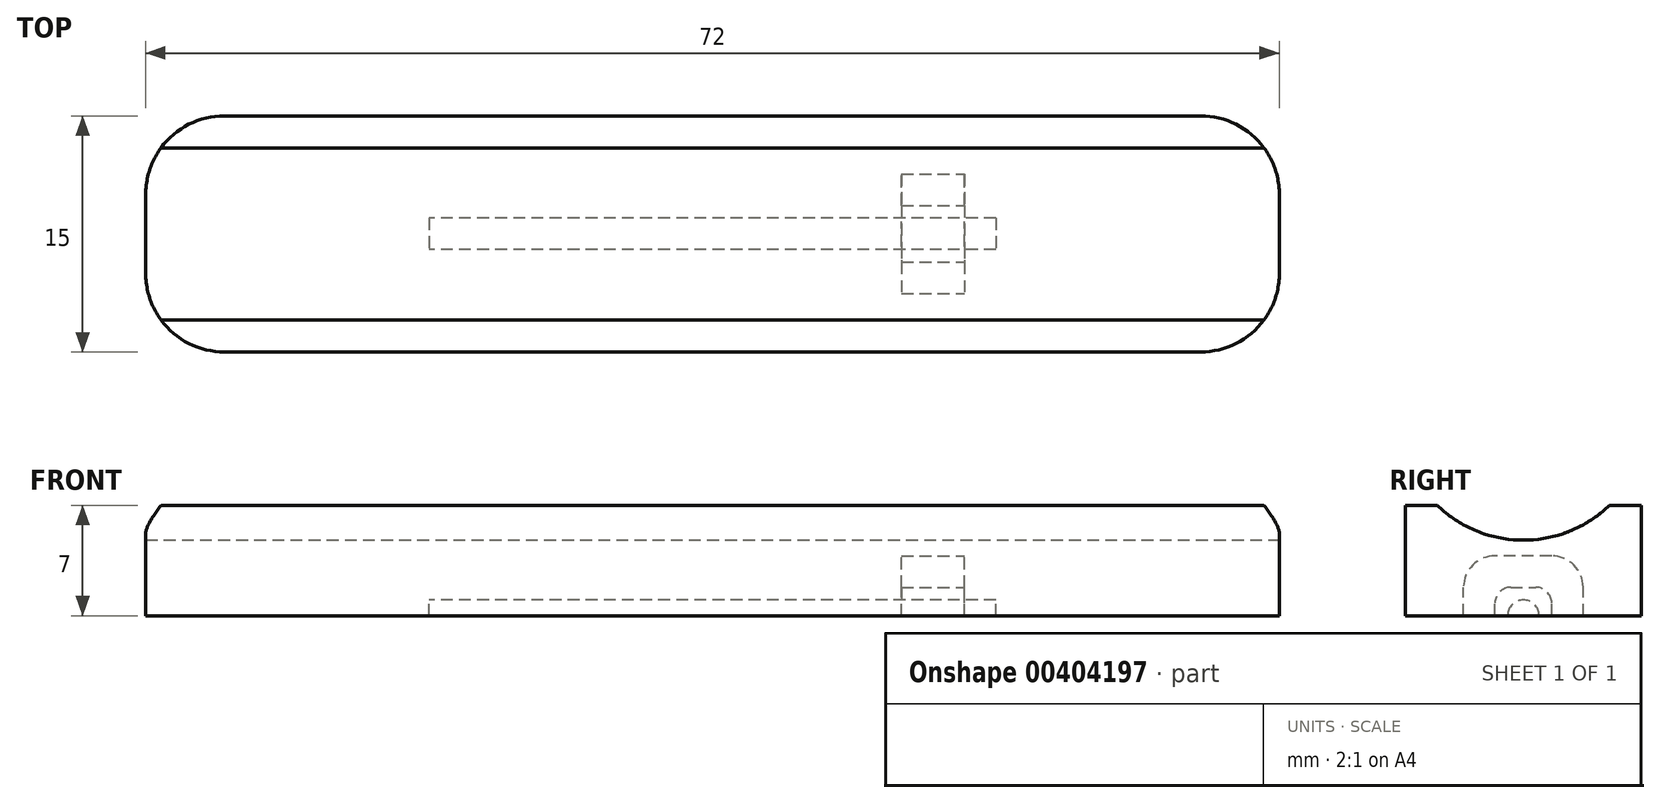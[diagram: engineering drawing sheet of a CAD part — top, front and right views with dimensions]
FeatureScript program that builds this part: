
annotation { "Feature Type Name" : "Feature", "Feature Type Description" : "" }
export const myFeature = defineFeature(function(context is Context, id is Id, definition is map)
    precondition{}
    {
        {
            var Q0;
            Q0=qCreatedBy(makeId("Top.planeOp"),FACE);
            var sketch = newSketch(context, id + "F0", { "sketchPlane" : qUnion([Q0])});
            skLineSegment(sketch, "E0.bottom", {"start": v(36, 7.5) * mm, "end": v(-36, 7.5) * mm});
            skLineSegment(sketch, "E0.top", {"start": v(36, -7.5) * mm, "end": v(-36, -7.5) * mm});
            skLineSegment(sketch, "E0.left", {"start": v(36, 7.5) * mm, "end": v(36, -7.5) * mm});
            skLineSegment(sketch, "E0.right", {"start": v(-36, 7.5) * mm, "end": v(-36, -7.5) * mm});
            skPoint(sketch, "E0.middle", {"position": v(0, 0) * mm});
            skLineSegment(sketch, "E1.bottom", {"start": v(42, 10.7) * mm, "end": v(2.77, 10.7) * mm, "construction": true});
            skLineSegment(sketch, "E1.top", {"start": v(42, -10.7) * mm, "end": v(23.2, -10.7) * mm, "construction": true});
            skLineSegment(sketch, "E1.left", {"start": v(42, 10.7) * mm, "end": v(42, 5.54) * mm, "construction": true});
            skLineSegment(sketch, "E1.right", {"start": v(-42, 10.7) * mm, "end": v(-42, 6.4) * mm, "construction": true});
            skCircle(sketch, "E2.cCircle", {"center": v(42, 0) * mm, "radius": 5.54 * mm, "construction": true});
            skPoint(sketch, "E2.cCircle.centerSnap0", {"position": v(42, 0) * mm});
            skLineSegment(sketch, "E2.0", {"start": v(47.54, 3.2) * mm, "end": v(47.54, -3.2) * mm, "construction": true});
            skLineSegment(sketch, "E2.1", {"start": v(47.54, -3.2) * mm, "end": v(42, -6.4) * mm, "construction": true});
            skLineSegment(sketch, "E2.2", {"start": v(42, -6.4) * mm, "end": v(36.46, -3.2) * mm, "construction": true});
            skLineSegment(sketch, "E2.3", {"start": v(36.46, -3.2) * mm, "end": v(36.46, 3.2) * mm, "construction": true});
            skLineSegment(sketch, "E2.4", {"start": v(36.46, 3.2) * mm, "end": v(42, 6.4) * mm, "construction": true});
            skLineSegment(sketch, "E2.5", {"start": v(42, 6.4) * mm, "end": v(47.54, 3.2) * mm, "construction": true});
            skPoint(sketch, "E2.0.midPoint", {"position": v(47.54, 0) * mm});
            skLineSegment(sketch, "E3.MirrorCS", {"start": v(-42, 6.4) * mm, "end": v(-47.54, 3.2) * mm, "construction": true});
            skLineSegment(sketch, "E4.MirrorCS", {"start": v(-47.54, 3.2) * mm, "end": v(-47.54, -3.2) * mm, "construction": true});
            skLineSegment(sketch, "E5.MirrorCS", {"start": v(-47.54, -3.2) * mm, "end": v(-42, -6.4) * mm, "construction": true});
            skLineSegment(sketch, "E6.trimOffspring", {"start": v(-42, -6.4) * mm, "end": v(-42, -10.7) * mm, "construction": true});
            skLineSegment(sketch, "E7.trimOffspring", {"start": v(42, -5.54) * mm, "end": v(42, -10.7) * mm, "construction": true});
            skCircle(sketch, "E8.cCircle", {"center": v(0, 10.7) * mm, "radius": 2.77 * mm, "construction": true});
            skLineSegment(sketch, "E8.0", {"start": v(-1.6, 13.47) * mm, "end": v(1.6, 13.47) * mm, "construction": true});
            skLineSegment(sketch, "E8.1", {"start": v(1.6, 13.47) * mm, "end": v(3.2, 10.7) * mm, "construction": true});
            skLineSegment(sketch, "E8.2", {"start": v(3.2, 10.7) * mm, "end": v(1.6, 7.93) * mm, "construction": true});
            skLineSegment(sketch, "E8.3", {"start": v(1.6, 7.93) * mm, "end": v(-1.6, 7.93) * mm, "construction": true});
            skLineSegment(sketch, "E8.4", {"start": v(-1.6, 7.93) * mm, "end": v(-3.2, 10.7) * mm, "construction": true});
            skLineSegment(sketch, "E8.5", {"start": v(-3.2, 10.7) * mm, "end": v(-1.6, 13.47) * mm, "construction": true});
            skPoint(sketch, "E8.0.midPoint", {"position": v(0, 13.47) * mm});
            skCircle(sketch, "E9.cCircle", {"center": v(-20, -10.7) * mm, "radius": 2.77 * mm, "construction": true});
            skLineSegment(sketch, "E9.0", {"start": v(-18.4, -13.47) * mm, "end": v(-21.6, -13.47) * mm, "construction": true});
            skLineSegment(sketch, "E9.1", {"start": v(-21.6, -13.47) * mm, "end": v(-23.2, -10.7) * mm, "construction": true});
            skLineSegment(sketch, "E9.2", {"start": v(-23.2, -10.7) * mm, "end": v(-21.6, -7.93) * mm, "construction": true});
            skLineSegment(sketch, "E9.3", {"start": v(-21.6, -7.93) * mm, "end": v(-18.4, -7.93) * mm, "construction": true});
            skLineSegment(sketch, "E9.4", {"start": v(-18.4, -7.93) * mm, "end": v(-16.8, -10.7) * mm, "construction": true});
            skLineSegment(sketch, "E9.5", {"start": v(-16.8, -10.7) * mm, "end": v(-18.4, -13.47) * mm, "construction": true});
            skPoint(sketch, "E9.0.midPoint", {"position": v(-20, -13.47) * mm});
            skLineSegment(sketch, "E10.MirrorCS", {"start": v(16.8, -10.7) * mm, "end": v(18.4, -13.47) * mm, "construction": true});
            skLineSegment(sketch, "E11.MirrorCS", {"start": v(21.6, -13.47) * mm, "end": v(23.2, -10.7) * mm, "construction": true});
            skLineSegment(sketch, "E12.MirrorCS", {"start": v(18.4, -13.47) * mm, "end": v(21.6, -13.47) * mm, "construction": true});
            skLineSegment(sketch, "E13.trimOffspring", {"start": v(16.8, -10.7) * mm, "end": v(-17.23, -10.7) * mm, "construction": true});
            skLineSegment(sketch, "E14.trimOffspring", {"start": v(-22.77, -10.7) * mm, "end": v(-42, -10.7) * mm, "construction": true});
            skLineSegment(sketch, "E15.trimOffspring", {"start": v(-2.77, 10.7) * mm, "end": v(-42, 10.7) * mm, "construction": true});
            skCircle(sketch, "E16", {"center": v(42, 0) * mm, "radius": 2.25 * mm, "construction": true});
            skCircle(sketch, "E17.MirrorC", {"center": v(-42, 0) * mm, "radius": 2.25 * mm, "construction": true});
            skSolve(sketch);
        }
        {
            var Q0;
            Q0=qSketchRegion(id+"F0",true);
            extrude(context, id + "F1", {"entities" : qUnion([Q0]), "depth" : 3.8 * mm});
        }
        {
            var Q0;
            Q0=makeQuery(id+"F1.opExtrude","SWEPT_FACE",FACE,{"disambiguationData":[OSD([sQuery(id+"F0.wireOp",EDGE,"E0.left")])]});
            var sketch = newSketch(context, id + "F2", { "sketchPlane" : qUnion([Q0])});
            skArc(sketch, "E18", {"start": v(5.46, 7) * mm, "mid": v(0, 4.8) * mm, "end": v(-5.46, 7) * mm});
            skLineSegment(sketch, "E19", {"start": v(-7.5, 3.8) * mm, "end": v(-7.5, 7) * mm});
            skLineSegment(sketch, "E20", {"start": v(-7.5, 7) * mm, "end": v(-5.46, 7) * mm});
            skLineSegment(sketch, "E21.MirrorCS", {"start": v(7.5, 7) * mm, "end": v(5.46, 7) * mm});
            skLineSegment(sketch, "E22.MirrorCS", {"start": v(7.5, 3.8) * mm, "end": v(7.5, 7) * mm});
            skLineSegment(sketch, "E23", {"start": v(-7.5, 3.8) * mm, "end": v(7.5, 3.8) * mm});
            skSolve(sketch);
        }
        {
            var Q0;
            Q0 = qSketchRegion(id + "F2", true);
            extrude(context, id + "F3", {"entities" : qUnion([Q0]), "operationType" : NewBodyOperationType.ADD, "oppositeDirection" : true, "depth" : 72 * mm});
        }
        {
            var Q0;
            Q0=makeQuery(id+"F1.opExtrude","SWEPT_EDGE",EDGE,{"disambiguationData":[OSD([sQuery(id+"F0.wireOp",EDGE,"E0.top"),sQuery(id+"F0.wireOp",EDGE,"E0.right")])]});
            var Q1;
            Q1=makeQuery(id+"F1.opExtrude","SWEPT_EDGE",EDGE,{"disambiguationData":[OSD([sQuery(id+"F0.wireOp",EDGE,"E0.top"),sQuery(id+"F0.wireOp",EDGE,"E0.left")])]});
            var Q2;
            Q2=makeQuery(id+"F1.opExtrude","SWEPT_EDGE",EDGE,{"disambiguationData":[OSD([sQuery(id+"F0.wireOp",EDGE,"E0.bottom"),sQuery(id+"F0.wireOp",EDGE,"E0.left")])]});
            var Q3;
            Q3=makeQuery(id+"F1.opExtrude","SWEPT_EDGE",EDGE,{"disambiguationData":[OSD([sQuery(id+"F0.wireOp",EDGE,"E0.bottom"),sQuery(id+"F0.wireOp",EDGE,"E0.right")])]});
            fillet(context, id + "F4", {"entities" : qUnion([Q0, Q1, Q2, Q3]), "radius" : 5 * mm, "tangentPropagation" : true, "allowEdgeOverflow" : false});
        }
        {
            var Q0;
            {var subQ0=sQuery(id+"F2.wireOp",EDGE,"E22.MirrorCS");var subQ1=makeQuery(id+"F3.opExtrude","SWEPT_FACE",FACE,{"disambiguationData":[OSD([subQ0])]});var subQ2=sQuery(id+"F2.wireOp",EDGE,"E19");var subQ3=makeQuery(id+"F3.opExtrude","SWEPT_FACE",FACE,{"disambiguationData":[OSD([subQ2])]});var subQ4=sQuery(id+"F0.wireOp",EDGE,"E0.top");var subQ5=makeQuery(id+"F1.opExtrude","SWEPT_FACE",FACE,{"disambiguationData":[OSD([subQ4])]});var subQ6=sQuery(id+"F0.wireOp",EDGE,"E0.bottom");var subQ7=makeQuery(id+"F1.opExtrude","SWEPT_FACE",FACE,{"disambiguationData":[OSD([subQ6])]});var subQ8=makeQuery(id+"FS2QGUQCjs8xVGR_2.opExtrude","SWEPT_FACE",FACE,{"disambiguationData":[OSD([sQuery(id+"F7LmlpVssTPIlAy_2.wireOp",EDGE,"s6dsamZl-Msn8-8iWp-o4xs-jUPkNgLWp00G")])]});var subQ9=makeQuery(id+"FS2QGUQCjs8xVGR_2.opExtrude","SWEPT_FACE",FACE,{"disambiguationData":[OSD([sQuery(id+"F7LmlpVssTPIlAy_2.wireOp",EDGE,"ca31c345-0968-45d3-b07e-e712e50a66631.MirrorCS")])]});var subQ10=sQuery(id+"F0.wireOp",EDGE,"E0.right");var subQ11=sQuery(id+"F0.wireOp",EDGE,"E0.left");var subQ12=makeQuery(id+"F1.opExtrude","CAP_FACE",FACE,{"disambiguationData":[OSD([subQ6,subQ4,subQ11,subQ10])],"isStart":true});var subQ13=sQuery(id+"F2.wireOp",EDGE,"E23");var subQ14=sQuery(id+"F2.wireOp",EDGE,"E21.MirrorCS");var subQ15=sQuery(id+"F2.wireOp",EDGE,"E20");var subQ16=sQuery(id+"F2.wireOp",EDGE,"E18");Q0=makeQuery(id+"FFu2NJl8xk8y0DB_2.boolean.opBoolean","MERGE",FACE,{"derivedFrom":[makeQuery(id+"FS2QGUQCjs8xVGR_2.boolean.opBoolean","SPLIT",FACE,{"disambiguationData":[TD([subQ7,subQ5,makeQuery(id+"F1.opExtrude","SWEPT_FACE",FACE,{"disambiguationData":[OSD([subQ11])]}),makeQuery(id+"F3.opExtrude","CAP_FACE",FACE,{"disambiguationData":[OSD([subQ16,subQ2,subQ15,subQ14,subQ0,subQ13])],"isStart":true}),subQ3,subQ1,makeQuery(id+"F4.opFillet","BLEND_FACE",FACE,{"disambiguationData":[OSD([subQ6,subQ11,subQ0])]}),makeQuery(id+"F4.opFillet","BLEND_FACE",FACE,{"disambiguationData":[OSD([subQ4,subQ11,subQ2])]}),subQ9])],"derivedFrom":subQ12}),makeQuery(id+"FS2QGUQCjs8xVGR_2.boolean.opBoolean","SPLIT",FACE,{"disambiguationData":[TD([subQ7,subQ5,makeQuery(id+"F1.opExtrude","SWEPT_FACE",FACE,{"disambiguationData":[OSD([subQ10])]}),makeQuery(id+"F3.opExtrude","CAP_FACE",FACE,{"disambiguationData":[OSD([subQ16,subQ2,subQ15,subQ14,subQ0,subQ13])],"isStart":false}),subQ3,subQ1,makeQuery(id+"F4.opFillet","BLEND_FACE",FACE,{"disambiguationData":[OSD([subQ6,subQ10,subQ0])]}),makeQuery(id+"F4.opFillet","BLEND_FACE",FACE,{"disambiguationData":[OSD([subQ4,subQ10,subQ2])]}),subQ8])],"derivedFrom":subQ12}),makeQuery(id+"FS2QGUQCjs8xVGR_2.boolean.opBoolean","SPLIT",FACE,{"disambiguationData":[TD([subQ7,subQ5,subQ3,subQ1,subQ8,subQ9])],"derivedFrom":subQ12}),makeQuery(id+"FFu2NJl8xk8y0DB_2.opExtrude","CAP_FACE",FACE,{"disambiguationData":[OSD([sQuery(id+"FllybTpC05ODztq_2.wireOp",EDGE,"f1PFnCn0-7IEy-hN21-08jR-4F1oPAhY7ZXU.bottom"),sQuery(id+"FllybTpC05ODztq_2.wireOp",EDGE,"f1PFnCn0-7IEy-hN21-08jR-4F1oPAhY7ZXU.top"),sQuery(id+"FllybTpC05ODztq_2.wireOp",EDGE,"f1PFnCn0-7IEy-hN21-08jR-4F1oPAhY7ZXU.left"),sQuery(id+"FllybTpC05ODztq_2.wireOp",EDGE,"f1PFnCn0-7IEy-hN21-08jR-4F1oPAhY7ZXU.right")])],"isStart":true}),makeQuery(id+"FFu2NJl8xk8y0DB_2.opExtrude","CAP_FACE",FACE,{"disambiguationData":[OSD([sQuery(id+"FllybTpC05ODztq_2.wireOp",EDGE,"dllZT7R5-8UqG-jUBg-xS9V-jZhT8ekEUGgy.bottom"),sQuery(id+"FllybTpC05ODztq_2.wireOp",EDGE,"dllZT7R5-8UqG-jUBg-xS9V-jZhT8ekEUGgy.top"),sQuery(id+"FllybTpC05ODztq_2.wireOp",EDGE,"dllZT7R5-8UqG-jUBg-xS9V-jZhT8ekEUGgy.left"),sQuery(id+"FllybTpC05ODztq_2.wireOp",EDGE,"dllZT7R5-8UqG-jUBg-xS9V-jZhT8ekEUGgy.right")])],"isStart":true})]});}
            var sketch = newSketch(context, id + "F5", { "sketchPlane" : qUnion([Q0])});
            skLineSegment(sketch, "E24.bottom", {"start": v(18, -1) * mm, "end": v(-18, -1) * mm});
            skLineSegment(sketch, "E24.top", {"start": v(18, 1) * mm, "end": v(-18, 1) * mm});
            skLineSegment(sketch, "E24.left", {"start": v(18, -1) * mm, "end": v(18, 1) * mm});
            skLineSegment(sketch, "E24.right", {"start": v(-18, -1) * mm, "end": v(-18, 1) * mm});
            skPoint(sketch, "E24.middle", {"position": v(0, 0) * mm});
            skSolve(sketch);
        }
        {
            var Q0;
            Q0 = qSketchRegion(id + "F5", true);
            extrude(context, id + "F6", {"entities" : qUnion([Q0]), "operationType" : NewBodyOperationType.REMOVE, "oppositeDirection" : true, "depth" : 1 * mm});
        }
        {
            var Q0;
            Q0=makeQuery(id+"F6.boolean.opBoolean","COPY",EDGE,{"derivedFrom":makeQuery(id+"F6.opExtrude","CAP_EDGE",EDGE,{"disambiguationData":[OSD([sQuery(id+"F5.wireOp",EDGE,"E24.top")])],"isStart":false})});
            var Q1;
            Q1=makeQuery(id+"F6.boolean.opBoolean","COPY",EDGE,{"derivedFrom":makeQuery(id+"F6.opExtrude","CAP_EDGE",EDGE,{"disambiguationData":[OSD([sQuery(id+"F5.wireOp",EDGE,"E24.bottom")])],"isStart":false})});
            fillet(context, id + "F7", {"entities" : qUnion([Q0, Q1]), "radius" : 1 * mm, "tangentPropagation" : true, "allowEdgeOverflow" : false});
        }
        {
            var Q0;
            Q0=qCreatedBy(makeId("Right.planeOp"),FACE);
            cPlane(context, id + "F8", {"entities" : qUnion([Q0]), "cplaneType" : CPlaneType.OFFSET, "offset" : 16 * mm, "width" : 150 * mm, "height" : 150 * mm});
        }
        {
            var Q0;
            Q0=qCreatedBy(id+"F8.planeOp",FACE);
            var sketch = newSketch(context, id + "F9", { "sketchPlane" : qUnion([Q0])});
            skLineSegment(sketch, "E25", {"start": v(-1.8, 0) * mm, "end": v(-1.8, 1.8) * mm});
            skLineSegment(sketch, "E26", {"start": v(-1.8, 1.8) * mm, "end": v(0, 1.8) * mm});
            skLineSegment(sketch, "E27", {"start": v(-1.8, 0) * mm, "end": v(-3.8, 0) * mm});
            skLineSegment(sketch, "E28", {"start": v(-3.8, 0) * mm, "end": v(-3.8, 3.8) * mm});
            skLineSegment(sketch, "E29", {"start": v(-3.8, 3.8) * mm, "end": v(0, 3.8) * mm});
            skLineSegment(sketch, "E30.MirrorCS", {"start": v(1.8, 0) * mm, "end": v(3.8, 0) * mm});
            skLineSegment(sketch, "E31.MirrorCS", {"start": v(1.8, 1.8) * mm, "end": v(0, 1.8) * mm});
            skLineSegment(sketch, "E32.MirrorCS", {"start": v(1.8, 0) * mm, "end": v(1.8, 1.8) * mm});
            skLineSegment(sketch, "E33.MirrorCS", {"start": v(3.8, 3.8) * mm, "end": v(0, 3.8) * mm});
            skLineSegment(sketch, "E34.MirrorCS", {"start": v(3.8, 0) * mm, "end": v(3.8, 3.8) * mm});
            skSolve(sketch);
        }
        {
            var Q0;
            Q0 = qSketchRegion(id + "F9", true);
            extrude(context, id + "F10", {"entities" : qUnion([Q0]), "operationType" : NewBodyOperationType.REMOVE, "oppositeDirection" : true, "depth" : 4 * mm});
        }
        {
            var Q0;
            Q0=makeQuery(id+"F10.boolean.opBoolean","COPY",EDGE,{"derivedFrom":makeQuery(id+"F10.opExtrude","SWEPT_EDGE",EDGE,{"disambiguationData":[OSD([sQuery(id+"F9.wireOp",EDGE,"E28"),sQuery(id+"F9.wireOp",EDGE,"E29")])]})});
            var Q1;
            Q1=makeQuery(id+"FTaxfMjI50FyExp_2.1.F10.boolean.opBoolean","COPY",EDGE,{"derivedFrom":makeQuery(id+"FTaxfMjI50FyExp_2.1.F10.opExtrude","SWEPT_EDGE",EDGE,{"disambiguationData":[OSD([sQuery(id+"F9.wireOp",EDGE,"E28"),sQuery(id+"F9.wireOp",EDGE,"E29")])]})});
            var Q2;
            Q2=makeQuery(id+"FTaxfMjI50FyExp_2.1.F10.boolean.opBoolean","COPY",EDGE,{"derivedFrom":makeQuery(id+"FTaxfMjI50FyExp_2.1.F10.opExtrude","SWEPT_EDGE",EDGE,{"disambiguationData":[OSD([sQuery(id+"F9.wireOp",EDGE,"E33.MirrorCS"),sQuery(id+"F9.wireOp",EDGE,"E34.MirrorCS")])]})});
            var Q3;
            Q3=makeQuery(id+"F10.boolean.opBoolean","COPY",EDGE,{"derivedFrom":makeQuery(id+"F10.opExtrude","SWEPT_EDGE",EDGE,{"disambiguationData":[OSD([sQuery(id+"F9.wireOp",EDGE,"E33.MirrorCS"),sQuery(id+"F9.wireOp",EDGE,"E34.MirrorCS")])]})});
            fillet(context, id + "F11", {"entities" : qUnion([Q0, Q1, Q2, Q3]), "radius" : 2 * mm, "tangentPropagation" : true, "allowEdgeOverflow" : false});
        }
        {
            var Q0;
            Q0=makeQuery(id+"F10.boolean.opBoolean","COPY",EDGE,{"derivedFrom":makeQuery(id+"F10.opExtrude","SWEPT_EDGE",EDGE,{"disambiguationData":[OSD([sQuery(id+"F9.wireOp",EDGE,"E25"),sQuery(id+"F9.wireOp",EDGE,"E26")])]})});
            var Q1;
            Q1=makeQuery(id+"F10.boolean.opBoolean","COPY",EDGE,{"derivedFrom":makeQuery(id+"F10.opExtrude","SWEPT_EDGE",EDGE,{"disambiguationData":[OSD([sQuery(id+"F9.wireOp",EDGE,"E31.MirrorCS"),sQuery(id+"F9.wireOp",EDGE,"E32.MirrorCS")])]})});
            var Q2;
            Q2=makeQuery(id+"FTaxfMjI50FyExp_2.1.F10.boolean.opBoolean","COPY",EDGE,{"derivedFrom":makeQuery(id+"FTaxfMjI50FyExp_2.1.F10.opExtrude","SWEPT_EDGE",EDGE,{"disambiguationData":[OSD([sQuery(id+"F9.wireOp",EDGE,"E31.MirrorCS"),sQuery(id+"F9.wireOp",EDGE,"E32.MirrorCS")])]})});
            var Q3;
            Q3=makeQuery(id+"FTaxfMjI50FyExp_2.1.F10.boolean.opBoolean","COPY",EDGE,{"derivedFrom":makeQuery(id+"FTaxfMjI50FyExp_2.1.F10.opExtrude","SWEPT_EDGE",EDGE,{"disambiguationData":[OSD([sQuery(id+"F9.wireOp",EDGE,"E25"),sQuery(id+"F9.wireOp",EDGE,"E26")])]})});
            fillet(context, id + "F12", {"entities" : qUnion([Q0, Q1, Q2, Q3]), "radius" : 1 * mm, "tangentPropagation" : true, "allowEdgeOverflow" : false});
        }
    });
